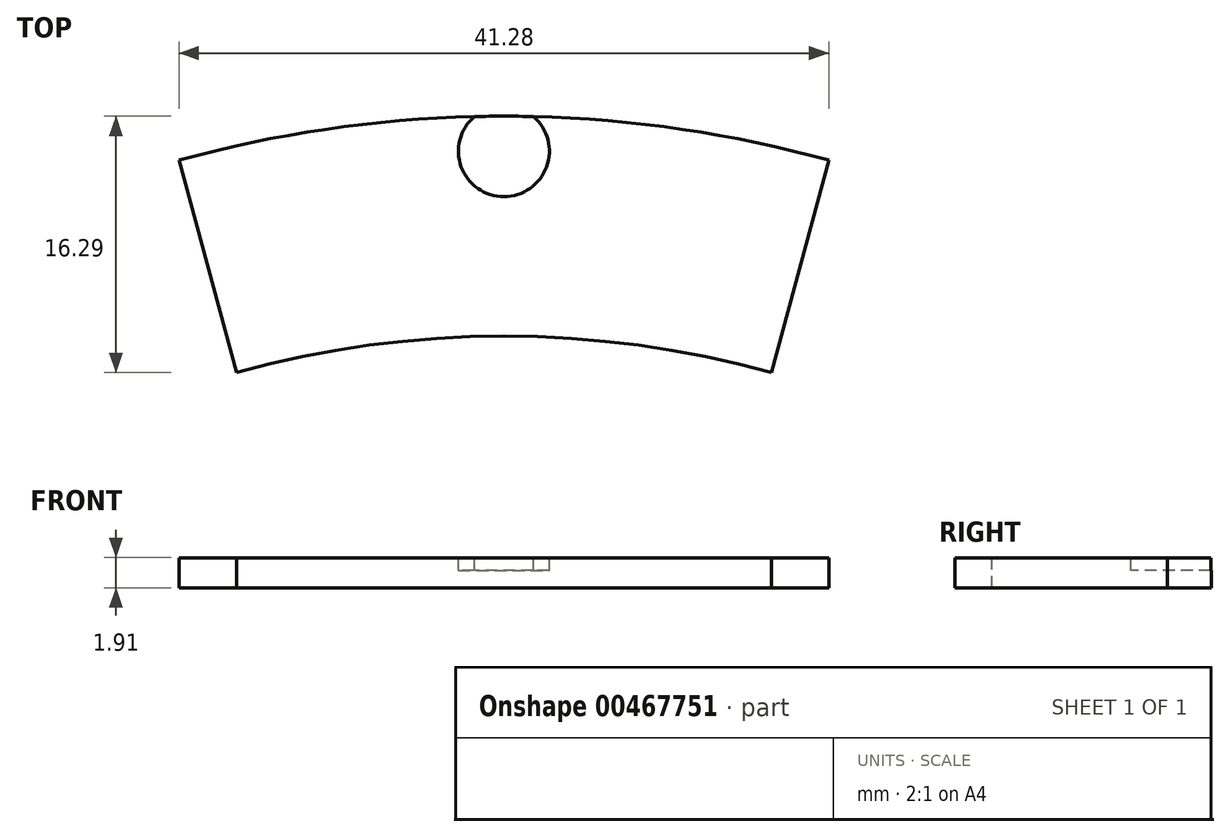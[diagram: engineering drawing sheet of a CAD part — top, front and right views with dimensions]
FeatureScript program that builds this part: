
annotation { "Feature Type Name" : "Feature", "Feature Type Description" : "" }
export const myFeature = defineFeature(function(context is Context, id is Id, definition is map)
    precondition{}
    {
        {
            var Q0;
            Q0=qCreatedBy(makeId("Top.planeOp"),FACE);
            var sketch = newSketch(context, id + "F0", { "sketchPlane" : qUnion([Q0])});
            skPoint(sketch, "E0.middle", {"position": v(0, 0) * mm});
            skArc(sketch, "E1", {"start": v(20.64, 4.82) * mm, "mid": v(0, 7.62) * mm, "end": v(-20.64, 4.82) * mm});
            skArc(sketch, "E2", {"start": v(17, -8.67) * mm, "mid": v(0, -6.35) * mm, "end": v(-17, -8.67) * mm});
            skLineSegment(sketch, "E3", {"start": v(-20.64, 4.82) * mm, "end": v(-20.64, -9.8) * mm, "construction": true});
            skLineSegment(sketch, "E4", {"start": v(20.64, -9.8) * mm, "end": v(20.64, 4.82) * mm, "construction": true});
            skLineSegment(sketch, "E5", {"start": v(-20.64, 4.82) * mm, "end": v(-17, -8.67) * mm});
            skLineSegment(sketch, "E6", {"start": v(20.64, 4.82) * mm, "end": v(17, -8.67) * mm});
            skSolve(sketch);
        }
        {
            var Q0;
            Q0 = qSketchRegion(id + "F0", true);
            extrude(context, id + "F1", {"entities" : qUnion([Q0]), "depth" : 1.9 * mm});
        }
        {
            var Q0;
            Q0=makeQuery(id+"F1.opExtrude","CAP_FACE",FACE,{"disambiguationData":[OSD([sQuery(id+"F0.wireOp",EDGE,"E1"),sQuery(id+"F0.wireOp",EDGE,"E2"),sQuery(id+"F0.wireOp",EDGE,"E3"),sQuery(id+"F0.wireOp",EDGE,"E4")])],"isStart":false});
            var sketch = newSketch(context, id + "F2", { "sketchPlane" : qUnion([Q0])});
            skCircle(sketch, "E7", {"center": v(0, 5.4) * mm, "radius": 2.89 * mm});
            skArc(sketch, "E8.0", {"start": v(20.64, 4.82) * mm, "mid": v(0, 7.62) * mm, "end": v(-20.64, 4.82) * mm, "construction": true});
            skArc(sketch, "E9", {"start": v(20.06, 2.68) * mm, "mid": v(0, 5.4) * mm, "end": v(-20.06, 2.68) * mm, "construction": true});
            skSolve(sketch);
        }
        {
            var Q0;
            Q0 = qSketchRegion(id + "F2", true);
            extrude(context, id + "F3", {"entities" : qUnion([Q0]), "operationType" : NewBodyOperationType.REMOVE, "oppositeDirection" : true, "depth" : 0.8 * mm});
        }
    });
